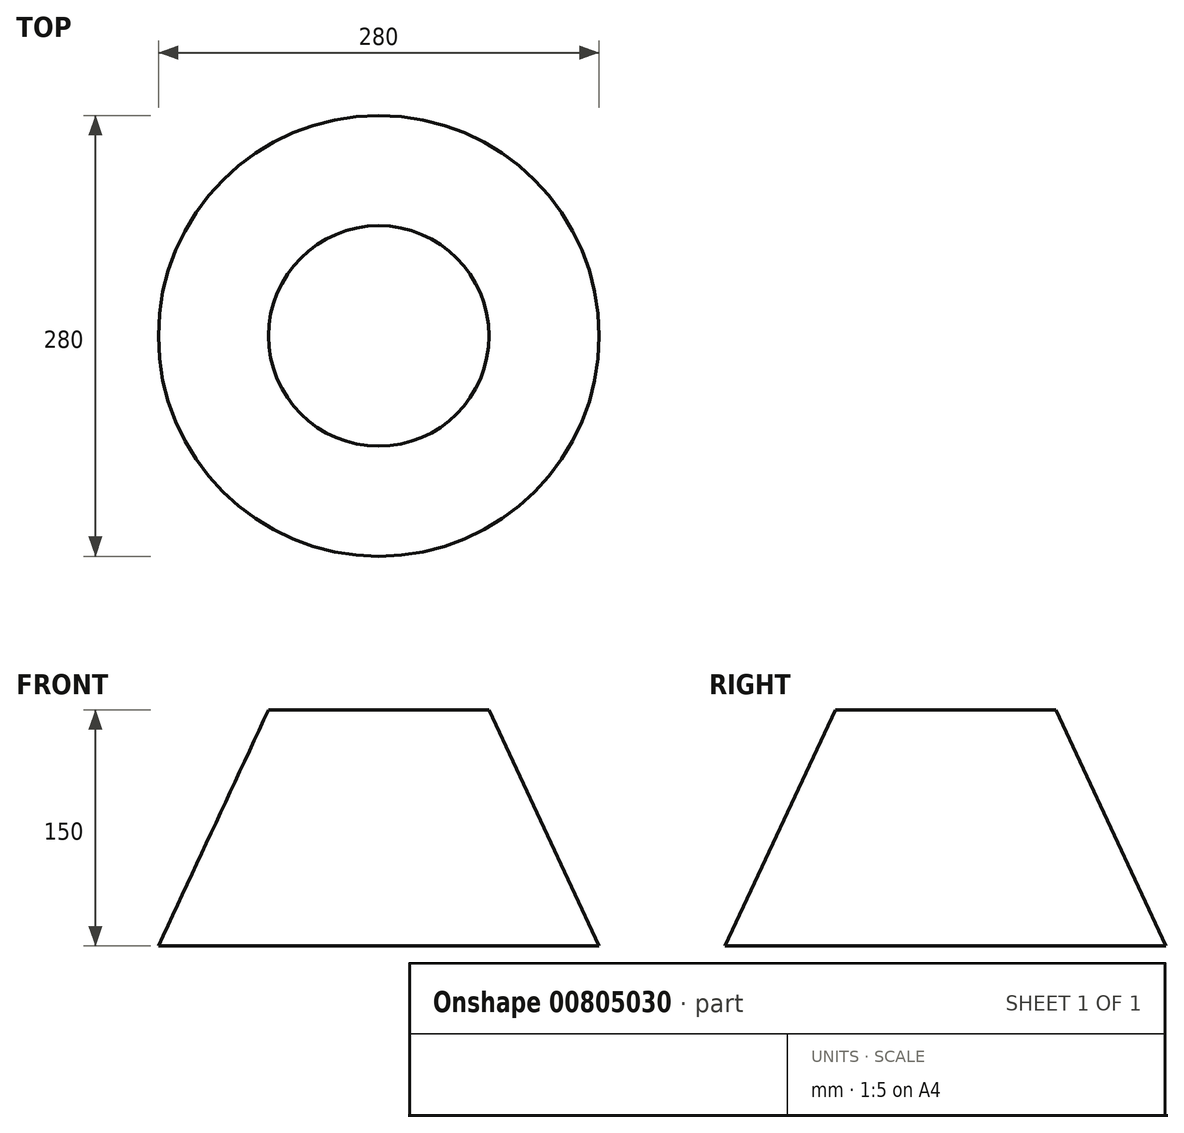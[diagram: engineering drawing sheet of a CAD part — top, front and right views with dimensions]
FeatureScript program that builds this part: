
annotation { "Feature Type Name" : "Feature", "Feature Type Description" : "" }
export const myFeature = defineFeature(function(context is Context, id is Id, definition is map)
    precondition{}
    {
        {
            var Q0;
            Q0=qCreatedBy(makeId("Front.planeOp"),FACE);
            var sketch = newSketch(context, id + "F0", { "sketchPlane" : qUnion([Q0])});
            skLineSegment(sketch, "E0", {"start": v(2.66, 0) * mm, "end": v(-140, 0) * mm});
            skLineSegment(sketch, "E1", {"start": v(-140, 0) * mm, "end": v(-70, 150) * mm});
            skLineSegment(sketch, "E2", {"start": v(-70, 150) * mm, "end": v(0, 150) * mm});
            skLineSegment(sketch, "E3", {"start": v(0, 150) * mm, "end": v(0, 0) * mm, "construction": true});
            skLineSegment(sketch, "E4", {"start": v(-140, 0) * mm, "end": v(0, 0) * mm});
            skSolve(sketch);
        }
        {
            var Q0;
            Q0=sQuery(id+"F0.wireOp",EDGE,"E1");
            var Q1;
            Q1=sQuery(id+"F0.wireOp",EDGE,"E3");
            revolve(context, id + "F1", {"bodyType" : ToolBodyType.SURFACE, "surfaceOperationType" : NewSurfaceOperationType.NEW, "surfaceEntities" : qUnion([Q0]), "axis" : qUnion([Q1]), "revolveType" : RevolveType.FULL});
        }
    });
